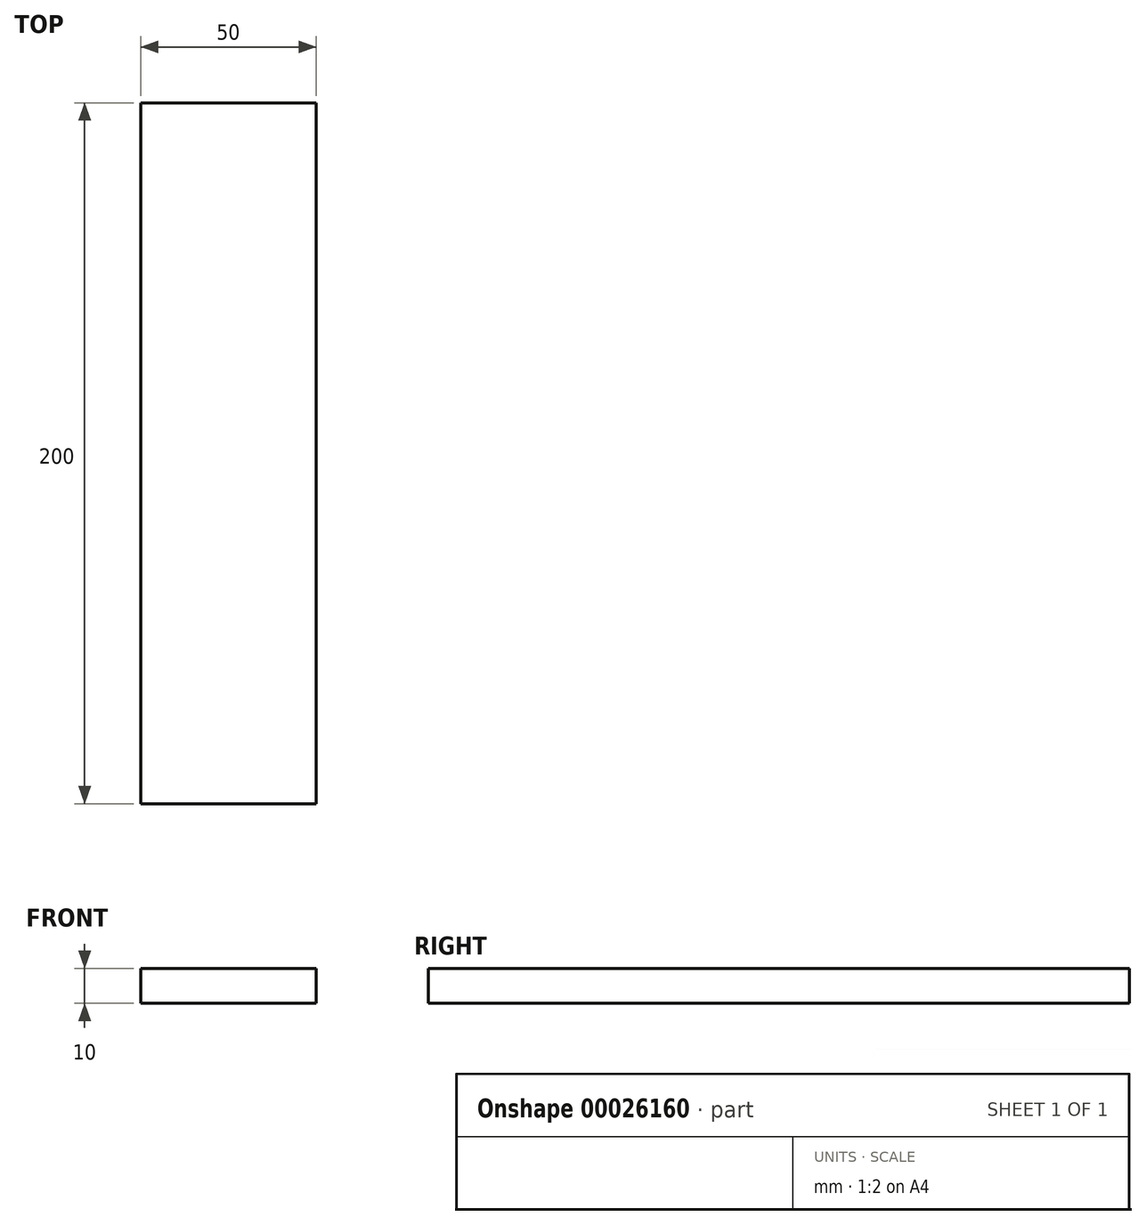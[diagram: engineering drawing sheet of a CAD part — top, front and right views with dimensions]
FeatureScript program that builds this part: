
annotation { "Feature Type Name" : "Feature", "Feature Type Description" : "" }
export const myFeature = defineFeature(function(context is Context, id is Id, definition is map)
    precondition{}
    {
        {
            var Q0;
            Q0=qCreatedBy(makeId("Top.planeOp"),FACE);
            var sketch = newSketch(context, id + "F0", { "sketchPlane" : qUnion([Q0])});
            skLineSegment(sketch, "E0.rect.bottom", {"start": v(-25, 100) * mm, "end": v(25, 100) * mm});
            skLineSegment(sketch, "E0.rect.top", {"start": v(-25, -100) * mm, "end": v(25, -100) * mm});
            skLineSegment(sketch, "E0.rect.left", {"start": v(-25, 100) * mm, "end": v(-25, -100) * mm});
            skLineSegment(sketch, "E0.rect.right", {"start": v(25, 100) * mm, "end": v(25, -100) * mm});
            skPoint(sketch, "E0.rect.middle", {"position": v(0, 0) * mm});
            skSolve(sketch);
        }
        {
            var Q0;
            Q0=makeQuery(id+"F0.imprint","IMPRINT",FACE,{"disambiguationData":[TD([[makeQuery(id+"F0.imprint","IMPRINT",EDGE,{"derivedFrom":sQuery(id+"F0.wireOp",EDGE,"E0.rect.bottom")}),-1.0]])]});
            extrude(context, id + "F1", {"entities" : qUnion([Q0]), "depth" : 10 * mm});
        }
    });
